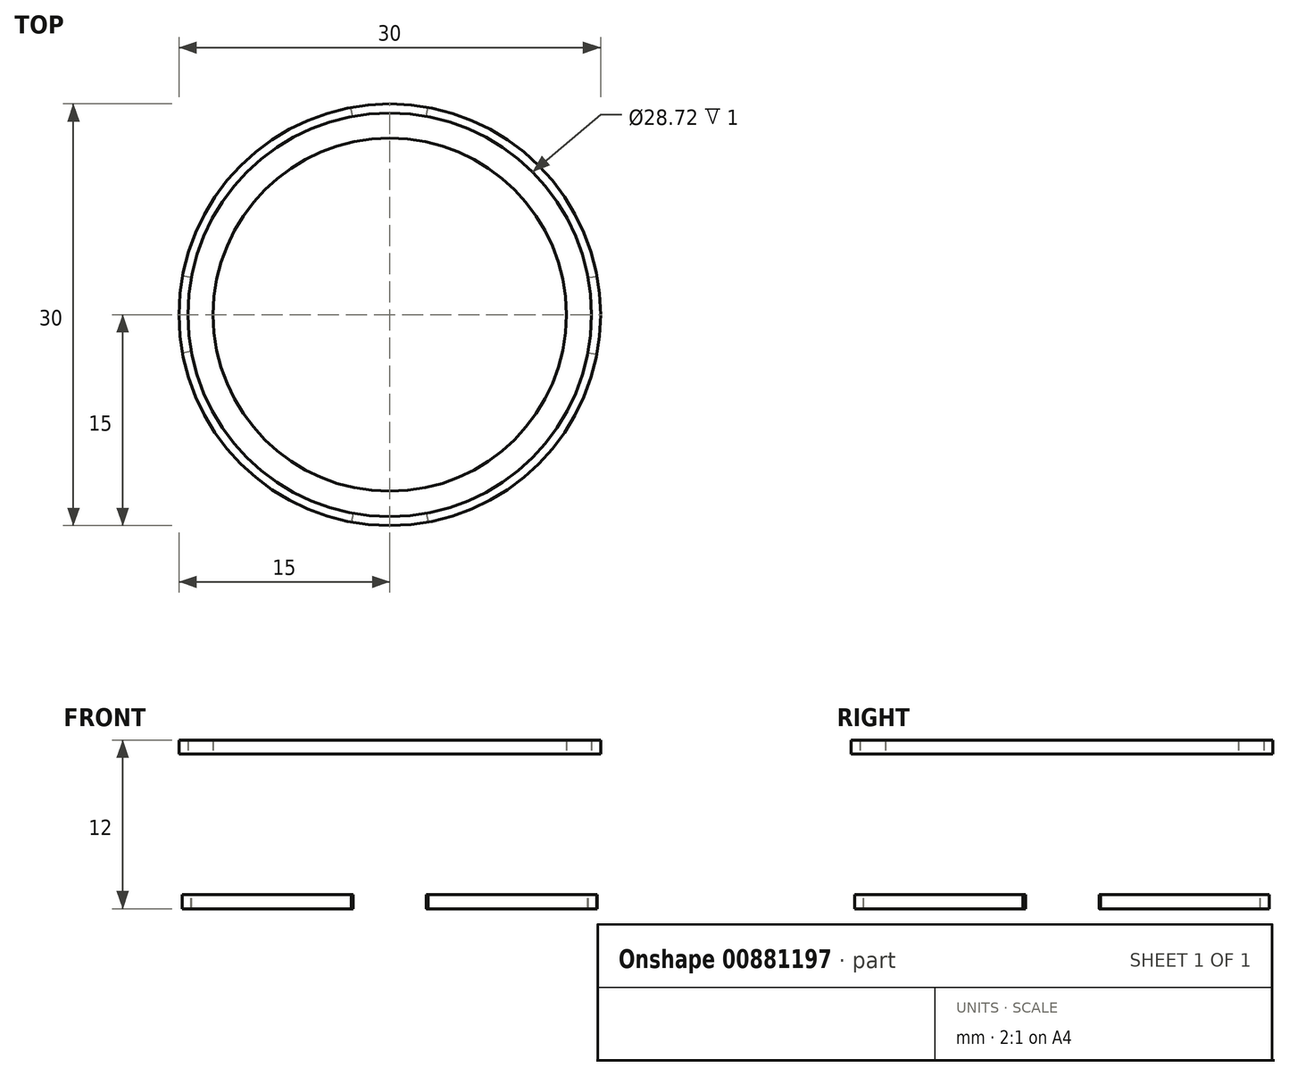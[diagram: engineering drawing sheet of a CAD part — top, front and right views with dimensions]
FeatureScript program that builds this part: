
annotation { "Feature Type Name" : "Feature", "Feature Type Description" : "" }
export const myFeature = defineFeature(function(context is Context, id is Id, definition is map)
    precondition{}
    {
        {
            var Q0;
            Q0=qCreatedBy(makeId("Top.planeOp"),FACE);
            var sketch = newSketch(context, id + "F0", { "sketchPlane" : qUnion([Q0])});
            skCircle(sketch, "E0", {"center": v(0, 0) * mm, "radius": 12.56 * mm});
            skCircle(sketch, "E1", {"center": v(0, 0) * mm, "radius": 14.36 * mm});
            skLineSegment(sketch, "E2", {"start": v(-13.13, 2.46) * mm, "end": v(-14.11, 2.65) * mm});
            skLineSegment(sketch, "E3", {"start": v(-12.35, -2.27) * mm, "end": v(-14.12, -2.6) * mm});
            skLineSegment(sketch, "E4", {"start": v(-2.43, 13.14) * mm, "end": v(-2.62, 14.12) * mm});
            skLineSegment(sketch, "E5", {"start": v(2.43, 13.14) * mm, "end": v(2.6, 14.12) * mm});
            skLineSegment(sketch, "E6", {"start": v(13.12, 2.54) * mm, "end": v(14.11, 2.66) * mm});
            skLineSegment(sketch, "E7", {"start": v(13.1, -2.59) * mm, "end": v(14.1, -2.7) * mm});
            skLineSegment(sketch, "E8", {"start": v(-2.43, -13.14) * mm, "end": v(-2.61, -14.12) * mm});
            skLineSegment(sketch, "E9", {"start": v(2.43, -13.14) * mm, "end": v(2.62, -14.12) * mm});
            skCircle(sketch, "E10", {"center": v(0, 0) * mm, "radius": 15 * mm});
            skLineSegment(sketch, "E11", {"start": v(-12.35, -2.27) * mm, "end": v(-14.75, -2.72) * mm});
            skLineSegment(sketch, "E12", {"start": v(-14.11, 2.65) * mm, "end": v(-12.34, 2.32) * mm});
            skLineSegment(sketch, "E13", {"start": v(-12.34, 2.32) * mm, "end": v(-14.11, 2.65) * mm});
            skLineSegment(sketch, "E14", {"start": v(-12.34, 2.32) * mm, "end": v(-14.74, 2.76) * mm});
            skLineSegment(sketch, "E15", {"start": v(-2.62, 14.12) * mm, "end": v(-2.27, 12.35) * mm});
            skLineSegment(sketch, "E16", {"start": v(-2.27, 12.35) * mm, "end": v(-2.75, 14.75) * mm});
            skLineSegment(sketch, "E17", {"start": v(2.6, 14.12) * mm, "end": v(2.29, 12.35) * mm});
            skLineSegment(sketch, "E18", {"start": v(2.29, 12.35) * mm, "end": v(2.72, 14.75) * mm});
            skLineSegment(sketch, "E19", {"start": v(14.11, 2.66) * mm, "end": v(12.32, 2.44) * mm});
            skLineSegment(sketch, "E20", {"start": v(12.32, 2.44) * mm, "end": v(14.75, 2.73) * mm});
            skLineSegment(sketch, "E21", {"start": v(14.1, -2.7) * mm, "end": v(12.31, -2.49) * mm});
            skLineSegment(sketch, "E22", {"start": v(12.31, -2.49) * mm, "end": v(14.74, -2.78) * mm});
            skLineSegment(sketch, "E23", {"start": v(2.62, -14.12) * mm, "end": v(2.29, -12.35) * mm});
            skLineSegment(sketch, "E24", {"start": v(2.29, -12.35) * mm, "end": v(2.73, -14.75) * mm});
            skLineSegment(sketch, "E25", {"start": v(-2.61, -14.12) * mm, "end": v(-2.29, -12.35) * mm});
            skLineSegment(sketch, "E26", {"start": v(-2.29, -12.35) * mm, "end": v(-2.72, -14.75) * mm});
            skSolve(sketch);
        }
        {
            var Q0;
            {var subQ0=sQuery(id+"F0.wireOp",EDGE,"E14");var subQ3=makeQuery(id+"F0.imprint","IMPRINT",VERTEX,{"derivedFrom":subQ0});Q0=makeQuery(id+"F0.imprint","IMPRINT",FACE,{"disambiguationData":[TD([[makeQuery(id+"F0.imprint","IMPRINT",EDGE,{"disambiguationData":[TD([[subQ3,1.0]])],"derivedFrom":subQ0}),-1.0]])]});}
            var Q1;
            {var subQ0=sQuery(id+"F0.wireOp",EDGE,"E16");var subQ1=makeQuery(id+"F0.imprint","IMPRINT",VERTEX,{"derivedFrom":subQ0});Q1=makeQuery(id+"F0.imprint","IMPRINT",FACE,{"disambiguationData":[TD([[makeQuery(id+"F0.imprint","IMPRINT",EDGE,{"disambiguationData":[TD([[subQ1,1.0]])],"derivedFrom":subQ0}),-1.0]])]});}
            var Q2;
            {var subQ0=sQuery(id+"F0.wireOp",EDGE,"E18");var subQ3=makeQuery(id+"F0.imprint","IMPRINT",VERTEX,{"derivedFrom":subQ0});Q2=makeQuery(id+"F0.imprint","IMPRINT",FACE,{"disambiguationData":[TD([[makeQuery(id+"F0.imprint","IMPRINT",EDGE,{"disambiguationData":[TD([[subQ3,1.0]])],"derivedFrom":subQ0}),-1.0]])]});}
            var Q3;
            {var subQ0=sQuery(id+"F0.wireOp",EDGE,"E20");var subQ1=makeQuery(id+"F0.imprint","IMPRINT",VERTEX,{"derivedFrom":subQ0});Q3=makeQuery(id+"F0.imprint","IMPRINT",FACE,{"disambiguationData":[TD([[makeQuery(id+"F0.imprint","IMPRINT",EDGE,{"disambiguationData":[TD([[subQ1,1.0]])],"derivedFrom":subQ0}),-1.0]])]});}
            var Q4;
            {var subQ0=sQuery(id+"F0.wireOp",EDGE,"E22");var subQ3=makeQuery(id+"F0.imprint","IMPRINT",VERTEX,{"derivedFrom":subQ0});Q4=makeQuery(id+"F0.imprint","IMPRINT",FACE,{"disambiguationData":[TD([[makeQuery(id+"F0.imprint","IMPRINT",EDGE,{"disambiguationData":[TD([[subQ3,1.0]])],"derivedFrom":subQ0}),-1.0]])]});}
            var Q5;
            {var subQ0=sQuery(id+"F0.wireOp",EDGE,"E24");var subQ1=makeQuery(id+"F0.imprint","IMPRINT",VERTEX,{"derivedFrom":subQ0});Q5=makeQuery(id+"F0.imprint","IMPRINT",FACE,{"disambiguationData":[TD([[makeQuery(id+"F0.imprint","IMPRINT",EDGE,{"disambiguationData":[TD([[subQ1,1.0]])],"derivedFrom":subQ0}),-1.0]])]});}
            var Q6;
            {var subQ3=sQuery(id+"F0.wireOp",EDGE,"E26");var subQ5=makeQuery(id+"F0.imprint","IMPRINT",VERTEX,{"derivedFrom":subQ3});Q6=makeQuery(id+"F0.imprint","IMPRINT",FACE,{"disambiguationData":[TD([[makeQuery(id+"F0.imprint","IMPRINT",EDGE,{"disambiguationData":[TD([[subQ5,1.0]])],"derivedFrom":subQ3}),-1.0]])]});}
            var Q7;
            {var subQ5=sQuery(id+"F0.wireOp",EDGE,"E14");var subQ7=makeQuery(id+"F0.imprint","IMPRINT",VERTEX,{"derivedFrom":subQ5});Q7=makeQuery(id+"F0.imprint","IMPRINT",FACE,{"disambiguationData":[TD([[makeQuery(id+"F0.imprint","IMPRINT",EDGE,{"disambiguationData":[TD([[subQ7,1.0]])],"derivedFrom":subQ5}),1.0]])]});}
            var Q8;
            {var subQ0=sQuery(id+"F0.wireOp",EDGE,"E0");var subQ4=makeQuery(id+"F0.imprint","INTERSECT",VERTEX,{"derivedFrom":[subQ0,sQuery(id+"F0.wireOp",EDGE,"E18")]});Q8=makeQuery(id+"F0.imprint","IMPRINT",FACE,{"disambiguationData":[TD([[makeQuery(id+"F0.imprint","IMPRINT",EDGE,{"disambiguationData":[TD([[subQ4,1.0]])],"derivedFrom":subQ0}),1.0]])]});}
            extrude(context, id + "F1", {"entities" : qUnion([Q0, Q1, Q2, Q3, Q4, Q5, Q6, Q7, Q8]), "depth" : 1 * mm, "offsetDistance" : 25 * mm});
        }
        {
            var Q0;
            {var subQ0=sQuery(id+"F0.wireOp",EDGE,"E22");var subQ3=makeQuery(id+"F0.imprint","IMPRINT",VERTEX,{"derivedFrom":subQ0});Q0=makeQuery(id+"F0.imprint","IMPRINT",FACE,{"disambiguationData":[TD([[makeQuery(id+"F0.imprint","IMPRINT",EDGE,{"disambiguationData":[TD([[subQ3,1.0]])],"derivedFrom":subQ0}),-1.0]])]});}
            var Q1;
            {var subQ3=sQuery(id+"F0.wireOp",EDGE,"E26");var subQ5=makeQuery(id+"F0.imprint","IMPRINT",VERTEX,{"derivedFrom":subQ3});Q1=makeQuery(id+"F0.imprint","IMPRINT",FACE,{"disambiguationData":[TD([[makeQuery(id+"F0.imprint","IMPRINT",EDGE,{"disambiguationData":[TD([[subQ5,1.0]])],"derivedFrom":subQ3}),-1.0]])]});}
            var Q2;
            {var subQ0=sQuery(id+"F0.wireOp",EDGE,"E14");var subQ3=makeQuery(id+"F0.imprint","IMPRINT",VERTEX,{"derivedFrom":subQ0});Q2=makeQuery(id+"F0.imprint","IMPRINT",FACE,{"disambiguationData":[TD([[makeQuery(id+"F0.imprint","IMPRINT",EDGE,{"disambiguationData":[TD([[subQ3,1.0]])],"derivedFrom":subQ0}),-1.0]])]});}
            var Q3;
            {var subQ0=sQuery(id+"F0.wireOp",EDGE,"E18");var subQ3=makeQuery(id+"F0.imprint","IMPRINT",VERTEX,{"derivedFrom":subQ0});Q3=makeQuery(id+"F0.imprint","IMPRINT",FACE,{"disambiguationData":[TD([[makeQuery(id+"F0.imprint","IMPRINT",EDGE,{"disambiguationData":[TD([[subQ3,1.0]])],"derivedFrom":subQ0}),-1.0]])]});}
            var Q4;
            {var subQ0=sQuery(id+"F0.wireOp",EDGE,"E11");var subQ1=sQuery(id+"F0.wireOp",EDGE,"E1");var subQ2=makeQuery(id+"F0.imprint","INTERSECT",VERTEX,{"derivedFrom":[subQ1,subQ0]});Q4=makeQuery(id+"F0.imprint","IMPRINT",FACE,{"disambiguationData":[TD([[makeQuery(id+"F0.imprint","IMPRINT",EDGE,{"disambiguationData":[TD([[subQ2,-1.0]])],"derivedFrom":subQ1}),-1.0]])]});}
            var Q5;
            {var subQ0=sQuery(id+"F0.wireOp",EDGE,"E16");var subQ1=sQuery(id+"F0.wireOp",EDGE,"E1");var subQ2=makeQuery(id+"F0.imprint","INTERSECT",VERTEX,{"derivedFrom":[subQ1,subQ0]});Q5=makeQuery(id+"F0.imprint","IMPRINT",FACE,{"disambiguationData":[TD([[makeQuery(id+"F0.imprint","IMPRINT",EDGE,{"disambiguationData":[TD([[subQ2,-1.0]])],"derivedFrom":subQ1}),-1.0]])]});}
            var Q6;
            {var subQ0=sQuery(id+"F0.wireOp",EDGE,"E24");var subQ1=sQuery(id+"F0.wireOp",EDGE,"E1");var subQ2=makeQuery(id+"F0.imprint","INTERSECT",VERTEX,{"derivedFrom":[subQ1,subQ0]});Q6=makeQuery(id+"F0.imprint","IMPRINT",FACE,{"disambiguationData":[TD([[makeQuery(id+"F0.imprint","IMPRINT",EDGE,{"disambiguationData":[TD([[subQ2,-1.0]])],"derivedFrom":subQ1}),-1.0]])]});}
            var Q7;
            {var subQ0=sQuery(id+"F0.wireOp",EDGE,"E18");var subQ1=sQuery(id+"F0.wireOp",EDGE,"E1");var subQ2=makeQuery(id+"F0.imprint","INTERSECT",VERTEX,{"derivedFrom":[subQ1,subQ0]});Q7=makeQuery(id+"F0.imprint","IMPRINT",FACE,{"disambiguationData":[TD([[makeQuery(id+"F0.imprint","IMPRINT",EDGE,{"disambiguationData":[TD([[subQ2,1.0]])],"derivedFrom":subQ1}),-1.0]])]});}
            extrude(context, id + "F2", {"entities" : qUnion([Q0, Q1, Q2, Q3, Q4, Q5, Q6, Q7]), "operationType" : NewBodyOperationType.ADD, "oppositeDirection" : true, "depth" : 11 * mm, "offsetDistance" : 25 * mm});
        }
        {
            var Q0;
            {var subQ0=sQuery(id+"F0.wireOp",EDGE,"E16");var subQ1=sQuery(id+"F0.wireOp",EDGE,"E1");var subQ2=makeQuery(id+"F0.imprint","INTERSECT",VERTEX,{"derivedFrom":[subQ1,subQ0]});Q0=makeQuery(id+"F0.imprint","IMPRINT",FACE,{"disambiguationData":[TD([[makeQuery(id+"F0.imprint","IMPRINT",EDGE,{"disambiguationData":[TD([[subQ2,-1.0]])],"derivedFrom":subQ1}),-1.0]])]});}
            var Q1;
            {var subQ0=sQuery(id+"F0.wireOp",EDGE,"E18");var subQ1=sQuery(id+"F0.wireOp",EDGE,"E1");var subQ2=makeQuery(id+"F0.imprint","INTERSECT",VERTEX,{"derivedFrom":[subQ1,subQ0]});Q1=makeQuery(id+"F0.imprint","IMPRINT",FACE,{"disambiguationData":[TD([[makeQuery(id+"F0.imprint","IMPRINT",EDGE,{"disambiguationData":[TD([[subQ2,1.0]])],"derivedFrom":subQ1}),-1.0]])]});}
            var Q2;
            {var subQ0=sQuery(id+"F0.wireOp",EDGE,"E24");var subQ1=sQuery(id+"F0.wireOp",EDGE,"E1");var subQ2=makeQuery(id+"F0.imprint","INTERSECT",VERTEX,{"derivedFrom":[subQ1,subQ0]});Q2=makeQuery(id+"F0.imprint","IMPRINT",FACE,{"disambiguationData":[TD([[makeQuery(id+"F0.imprint","IMPRINT",EDGE,{"disambiguationData":[TD([[subQ2,-1.0]])],"derivedFrom":subQ1}),-1.0]])]});}
            var Q3;
            {var subQ0=sQuery(id+"F0.wireOp",EDGE,"E11");var subQ1=sQuery(id+"F0.wireOp",EDGE,"E1");var subQ2=makeQuery(id+"F0.imprint","INTERSECT",VERTEX,{"derivedFrom":[subQ1,subQ0]});Q3=makeQuery(id+"F0.imprint","IMPRINT",FACE,{"disambiguationData":[TD([[makeQuery(id+"F0.imprint","IMPRINT",EDGE,{"disambiguationData":[TD([[subQ2,-1.0]])],"derivedFrom":subQ1}),-1.0]])]});}
            extrude(context, id + "F3", {"entities" : qUnion([Q0, Q1, Q2, Q3]), "operationType" : NewBodyOperationType.REMOVE, "oppositeDirection" : true, "depth" : 10 * mm, "offsetDistance" : 25 * mm});
        }
    });
